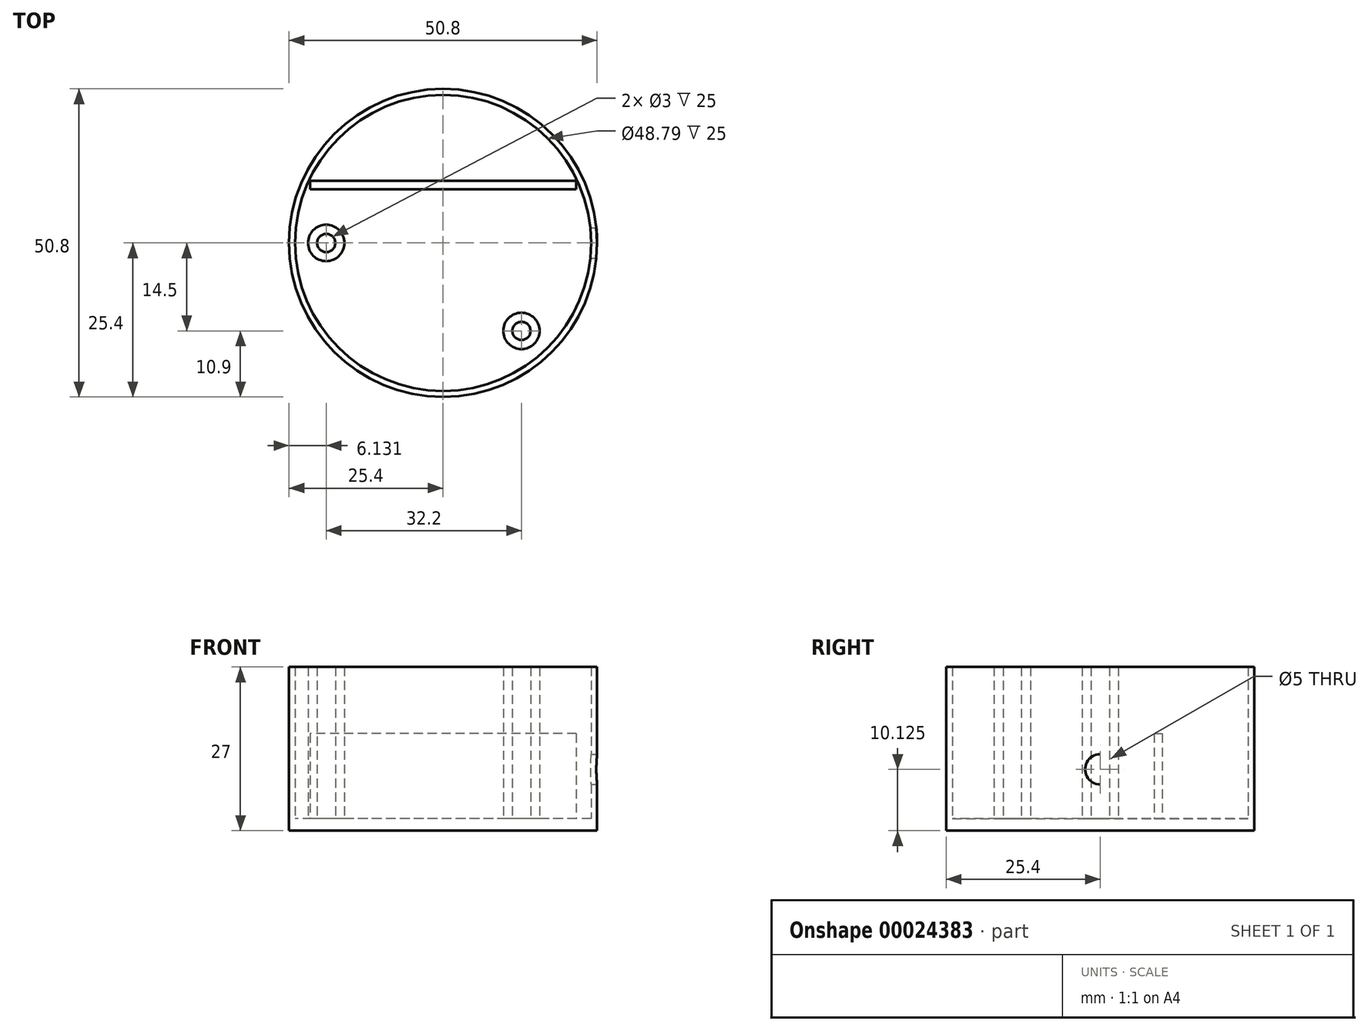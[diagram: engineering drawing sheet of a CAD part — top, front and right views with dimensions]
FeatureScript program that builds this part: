
annotation { "Feature Type Name" : "Feature", "Feature Type Description" : "" }
export const myFeature = defineFeature(function(context is Context, id is Id, definition is map)
    precondition{}
    {
        {
            var Q0;
            Q0=qCreatedBy(makeId("Top.planeOp"),FACE);
            var sketch = newSketch(context, id + "F0", { "sketchPlane" : qUnion([Q0])});
            skCircle(sketch, "E0", {"center": v(0, 0) * mm, "radius": 25.4 * mm});
            skSolve(sketch);
        }
        {
            var Q0;
            Q0=makeQuery(id+"F0.imprint","IMPRINT",FACE,{"disambiguationData":[TD([[makeQuery(id+"F0.imprint","IMPRINT",EDGE,{"derivedFrom":sQuery(id+"F0.wireOp",EDGE,"E0")}),1.0]])]});
            extrude(context, id + "F1", {"entities" : qUnion([Q0]), "oppositeDirection" : true, "depth" : 2 * mm});
        }
        {
            var Q0;
            Q0=makeQuery(id+"F0.imprint","IMPRINT",FACE,{"disambiguationData":[TD([[makeQuery(id+"F0.imprint","IMPRINT",EDGE,{"derivedFrom":sQuery(id+"F0.wireOp",EDGE,"E0")}),1.0]])]});
            var sketch = newSketch(context, id + "F2", { "sketchPlane" : qUnion([Q0])});
            skCircle(sketch, "E1", {"center": v(0, 0) * mm, "radius": 25.4 * mm});
            skSolve(sketch);
        }
        {
            var Q0;
            Q0=makeQuery(id+"F0.imprint","IMPRINT",FACE,{"disambiguationData":[TD([[makeQuery(id+"F0.imprint","IMPRINT",EDGE,{"derivedFrom":sQuery(id+"F0.wireOp",EDGE,"E0")}),1.0]])]});
            var sketch = newSketch(context, id + "F3", { "sketchPlane" : qUnion([Q0])});
            skCircle(sketch, "E2", {"center": v(0, 0) * mm, "radius": 24.4 * mm});
            skSolve(sketch);
        }
        {
            var Q0;
            Q0=makeQuery(id+"F3.imprint","IMPRINT",FACE,{"disambiguationData":[TD([[makeQuery(id+"F3.imprint","IMPRINT",EDGE,{"derivedFrom":sQuery(id+"F3.wireOp",EDGE,"E2")}),-1.0]])]});
            extrude(context, id + "F4", {"entities" : qUnion([Q0]), "operationType" : NewBodyOperationType.ADD, "depth" : 25 * mm});
        }
        {
            var Q0;
            Q0=qCreatedBy(makeId("Right.planeOp"),FACE);
            cPlane(context, id + "F5", {"entities" : qUnion([Q0]), "cplaneType" : CPlaneType.OFFSET, "offset" : 25.4 * mm, "width" : 152.4 * mm, "height" : 152.4 * mm});
        }
        {
            var Q0;
            Q0=qCreatedBy(id+"F5.planeOp",FACE);
            var sketch = newSketch(context, id + "F6", { "sketchPlane" : qUnion([Q0])});
            skCircle(sketch, "E3", {"center": v(0, 8.12) * mm, "radius": 5 * mm});
            skSolve(sketch);
        }
        {
            var Q0;
            Q0=sQuery(id+"F6.wireOp",VERTEX,"E3.center");
            var Q1;
            Q1=makeQuery(id+"F1.opExtrude","SWEPT_BODY",BODY,{"disambiguationData":[OSD([sQuery(id+"F0.wireOp",EDGE,"E0")])]});
            hole(context, id + "F7", {"style" : HoleStyle.SIMPLE, "holeDiameter" : 5 * mm, "endStyle" : HoleEndStyle.BLIND, "holeDepth" : 4 * mm, "locations" : qUnion([Q0]), "scope" : qUnion([Q1])});
        }
        {
            var Q0;
            Q0=makeQuery(id+"F3.imprint","IMPRINT",FACE,{"disambiguationData":[TD([[makeQuery(id+"F3.imprint","IMPRINT",EDGE,{"derivedFrom":sQuery(id+"F3.wireOp",EDGE,"E2")}),1.0]])]});
            var sketch = newSketch(context, id + "F8", { "sketchPlane" : qUnion([Q0])});
            skLineSegment(sketch, "E4.rect.bottom", {"start": v(21.96, 8.85) * mm, "end": v(-21.96, 8.85) * mm});
            skLineSegment(sketch, "E4.rect.top", {"start": v(21.96, 10.22) * mm, "end": v(-21.96, 10.22) * mm});
            skLineSegment(sketch, "E4.rect.left", {"start": v(21.96, 8.85) * mm, "end": v(21.96, 10.22) * mm});
            skLineSegment(sketch, "E4.rect.right", {"start": v(-21.96, 8.85) * mm, "end": v(-21.96, 10.22) * mm});
            skPoint(sketch, "E4.rect.middle", {"position": v(0, 9.54) * mm});
            skSolve(sketch);
        }
        {
            var Q0;
            Q0 = qSketchRegion(id + "F8", true);
            extrude(context, id + "F9", {"entities" : qUnion([Q0]), "operationType" : NewBodyOperationType.ADD, "depth" : 14 * mm});
        }
        {
            var Q0;
            Q0=makeQuery(id+"F3.imprint","IMPRINT",FACE,{"disambiguationData":[TD([[makeQuery(id+"F3.imprint","IMPRINT",EDGE,{"derivedFrom":sQuery(id+"F3.wireOp",EDGE,"E2")}),1.0]])]});
            var sketch = newSketch(context, id + "F10", { "sketchPlane" : qUnion([Q0])});
            skCircle(sketch, "E5", {"center": v(-19.27, 0) * mm, "radius": 3 * mm});
            skCircle(sketch, "E6", {"center": v(-19.27, 0) * mm, "radius": 1.5 * mm});
            skSolve(sketch);
        }
        {
            var Q0;
            Q0 = qSketchRegion(id + "F10", true);
            extrude(context, id + "F11", {"entities" : qUnion([Q0]), "operationType" : NewBodyOperationType.ADD, "depth" : 25 * mm});
        }
        {
            var Q0;
            Q0=makeQuery(id+"F2.imprint","IMPRINT",FACE,{"disambiguationData":[TD([[makeQuery(id+"F2.imprint","IMPRINT",EDGE,{"derivedFrom":sQuery(id+"F2.wireOp",EDGE,"E1")}),1.0]])]});
            var sketch = newSketch(context, id + "F12", { "sketchPlane" : qUnion([Q0])});
            skCircle(sketch, "E7", {"center": v(12.93, -14.5) * mm, "radius": 3 * mm});
            skCircle(sketch, "E8", {"center": v(12.93, -14.5) * mm, "radius": 1.5 * mm});
            skSolve(sketch);
        }
        {
            var Q0;
            Q0 = qSketchRegion(id + "F12", true);
            extrude(context, id + "F13", {"entities" : qUnion([Q0]), "operationType" : NewBodyOperationType.ADD, "depth" : 25 * mm});
        }
    });
